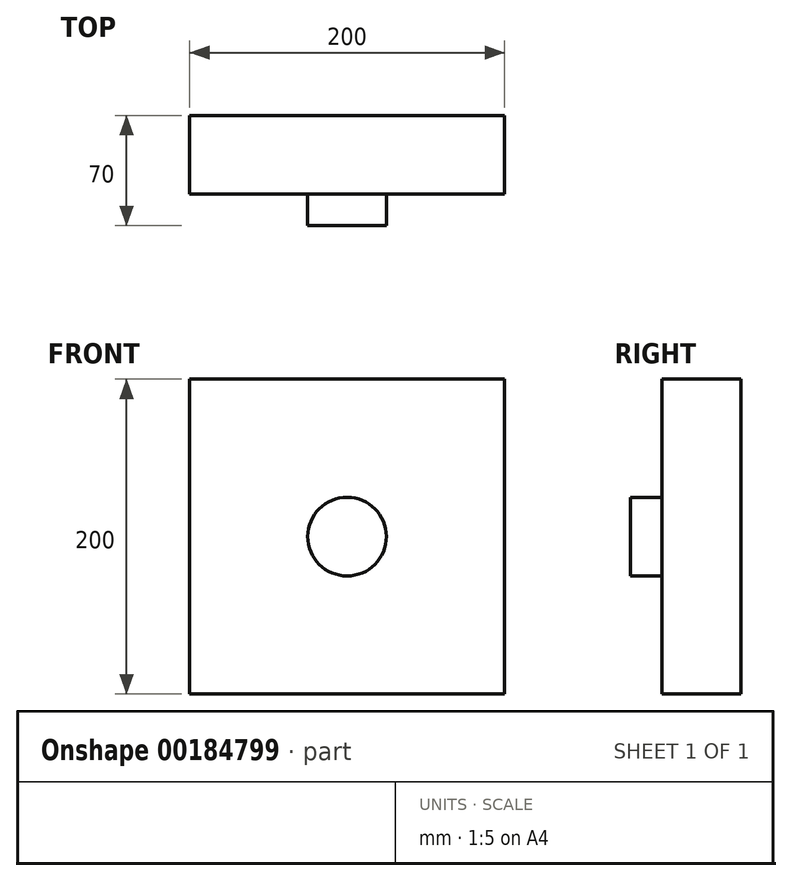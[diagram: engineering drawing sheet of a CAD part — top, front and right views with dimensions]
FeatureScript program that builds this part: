
annotation { "Feature Type Name" : "Feature", "Feature Type Description" : "" }
export const myFeature = defineFeature(function(context is Context, id is Id, definition is map)
    precondition{}
    {
        {
            var Q0;
            Q0=qCreatedBy(makeId("Front.planeOp"),FACE);
            var sketch = newSketch(context, id + "F0", { "sketchPlane" : qUnion([Q0])});
            skLineSegment(sketch, "E0.bottom", {"start": v(0, 0) * mm, "end": v(200, 0) * mm});
            skLineSegment(sketch, "E0.top", {"start": v(0, 200) * mm, "end": v(200, 200) * mm});
            skLineSegment(sketch, "E0.left", {"start": v(0, 0) * mm, "end": v(0, 200) * mm});
            skLineSegment(sketch, "E0.right", {"start": v(200, 0) * mm, "end": v(200, 200) * mm});
            skLineSegment(sketch, "E1", {"start": v(0, 105.33) * mm, "end": v(200, 105.33) * mm, "construction": true});
            skLineSegment(sketch, "E2", {"start": v(100, 200) * mm, "end": v(100, 0) * mm, "construction": true});
            skSolve(sketch);
        }
        {
            var Q0;
            Q0=makeQuery(id+"F0.imprint","IMPRINT",FACE,{"disambiguationData":[TD([[makeQuery(id+"F0.imprint","IMPRINT",EDGE,{"derivedFrom":sQuery(id+"F0.wireOp",EDGE,"E0.bottom")}),1.0]])]});
            extrude(context, id + "F1", {"entities" : qUnion([Q0]), "depth" : 50 * mm});
        }
        {
            var Q0;
            Q0=makeQuery(id+"F1.opExtrude","CAP_FACE",FACE,{"disambiguationData":[OSD([sQuery(id+"F0.wireOp",EDGE,"E0.bottom"),sQuery(id+"F0.wireOp",EDGE,"E0.top"),sQuery(id+"F0.wireOp",EDGE,"E0.left"),sQuery(id+"F0.wireOp",EDGE,"E0.right")])],"isStart":false});
            var sketch = newSketch(context, id + "F2", { "sketchPlane" : qUnion([Q0])});
            skLineSegment(sketch, "E3", {"start": v(0, 100) * mm, "end": v(200, 100) * mm, "construction": true});
            skLineSegment(sketch, "E4", {"start": v(100, 200) * mm, "end": v(100, 0) * mm, "construction": true});
            skCircle(sketch, "E5", {"center": v(100, 100) * mm, "radius": 25 * mm});
            skSolve(sketch);
        }
        {
            var Q0;
            Q0=makeQuery(id+"F2.imprint","IMPRINT",FACE,{"disambiguationData":[TD([[makeQuery(id+"F2.imprint","IMPRINT",EDGE,{"derivedFrom":sQuery(id+"F2.wireOp",EDGE,"E5")}),1.0]])]});
            extrude(context, id + "F3", {"entities" : qUnion([Q0]), "operationType" : NewBodyOperationType.ADD, "depth" : 20 * mm});
        }
    });
